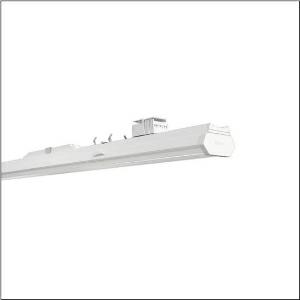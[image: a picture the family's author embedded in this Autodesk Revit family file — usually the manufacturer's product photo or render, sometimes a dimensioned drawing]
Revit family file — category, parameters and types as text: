
# Revit family: licross_r__11_protected_ho_51td1bdn4e5m_8869
name_source: partatom
category: Lighting Fixtures
units: mm (PartAtom-declared; Revit-internal decimal feet)

## family parameters
Cut with Voids When Loaded = No
Host = Face
Light Source = No
Part Type = Normal
Room Calculation Point = No
Round Connector Dimension = Use Diameter
Shared = No

## types (1)
- --- (1 x LED, 14500 lm, 87.3 W, 4000K)
    Apparent Load = 87 VA
    CIE Flux Codes = 54 82 95 97 100
    Color Rendering = 80
    Color Temperature = 4000K
    Default Elevation = 1800 mm
    Description = Licross® 11 Protected HO, luminaire insert, of sheet steel, galvanised, coil coated, white, length: 1.500mm, width: 90mm, height: 101mm, LED rated luminous flux: 14.500lm, light colour: 840, control gear: DALI 2, with plug, 5-pole, with phase selection, mains connection: 220..240V, AC, 50/60Hz, rated input power: 87W, halogen-free wiring, primary optical cover: cover, of PMMA, light emission: direct distribution, primary light characteristic: symmetric, protection rating (complete): IP54, insulation class (complete): insulation class I (protective earthing), certification: CE, ENEC, VDE, UKCA, protection symbol: D if used in an environment with non-conductive dust loads with corresponding accessories, impact resistance: IK06, permissible ambient temperature for indoor applications: -25..+30°C, corresponds to IFS (International Featured Standards) requirements for safety and quality in the food industry, reducing of maximum allowable ambient temperature of 5°C with ceiling mounting, LABS conformity tested according to VDMA 24364:2018-05, packaging unit: 1 piece
    Height = 92 mm
    Lamp = 1 x LED
    Lamp Light Flux = 14500 lm
    Lamp Power = 87.3 W
    Lamp count = 1
    Length = 1500 mm
    Luminous efficacy = 166 lm/W
    Manufacturer = Siteco
    ModVariant = No
    Model = 51TD1BDN4E5M
    Mounting Place = Ceiling
    Mounting Type = Pendant
    Number of Poles = 1
    OnlyDefault = Yes
    Power Factor = 1
    Product Name = Licross® 11 Protected HO
    Product group = luminaire insert
    ProductGroupID = 902
    Protection Class = Protection class I
    Protection Degree = IP 54
    RLX_Detail_Level = 1
    RLX_Emergency_Light_Flux = 0 lm
    RLX_Emergency_Type = 0
    RLX_Emergency_Type_DB = No
    RlxData = <blob elided: 24221 chars, md5=8a21e23c>
    Socket = socket
    Standby Power = 0 W
    System Light Flux = 14500 lm
    System Power = 87 W
    Type Comments = factory setting: luminous flux: 100 % | dim-lin: 254 | 589 mA
    Type Image = l_1256145.jpg
    URL = http://relux.com
    VarID = @adj_010809
    Voltage = 0 V
    Weight = 0.00 kg
    Width = 88 mm

## geometry (parser evidence)
native form markers: Blend x4, Sweep x11
no freeform markers — native parametric forms only
